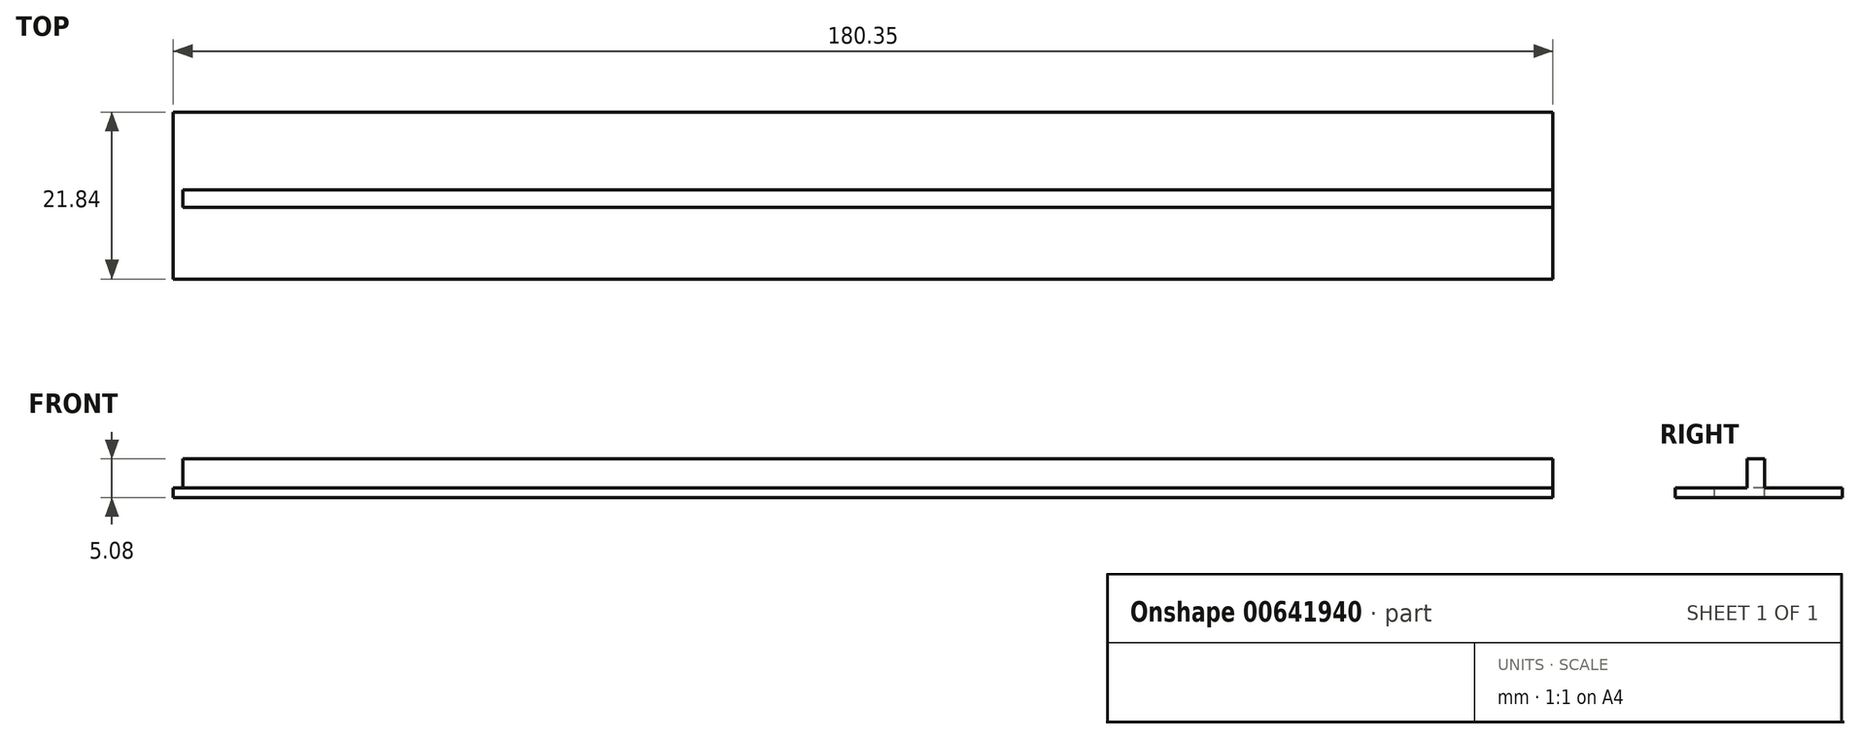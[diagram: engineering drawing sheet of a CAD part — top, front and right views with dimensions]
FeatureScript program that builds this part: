
annotation { "Feature Type Name" : "Feature", "Feature Type Description" : "" }
export const myFeature = defineFeature(function(context is Context, id is Id, definition is map)
    precondition{}
    {
        {
            var Q0;
            Q0=qCreatedBy(makeId("Front.planeOp"),FACE);
            var sketch = newSketch(context, id + "F0", { "sketchPlane" : qUnion([Q0])});
            skLineSegment(sketch, "E0.bottom", {"start": v(107.95, -50.8) * mm, "end": v(-107.95, -50.8) * mm});
            skLineSegment(sketch, "E0.top", {"start": v(107.95, 50.8) * mm, "end": v(-107.95, 50.8) * mm});
            skLineSegment(sketch, "E0.left", {"start": v(107.95, -50.8) * mm, "end": v(107.95, 50.8) * mm});
            skLineSegment(sketch, "E0.right", {"start": v(-107.95, -50.8) * mm, "end": v(-107.95, 50.8) * mm});
            skPoint(sketch, "E0.middle", {"position": v(0, 0) * mm});
            skLineSegment(sketch, "E1.bottom", {"start": v(88.9, -31.75) * mm, "end": v(-88.9, -31.75) * mm});
            skLineSegment(sketch, "E1.top", {"start": v(88.9, 31.75) * mm, "end": v(-88.9, 31.75) * mm});
            skLineSegment(sketch, "E1.left", {"start": v(88.9, -31.75) * mm, "end": v(88.9, 31.75) * mm});
            skLineSegment(sketch, "E1.right", {"start": v(-88.9, -31.75) * mm, "end": v(-88.9, 31.75) * mm});
            skSolve(sketch);
        }
        {
            var Q0;
            Q0=makeQuery(id+"F0.imprint","IMPRINT",FACE,{"disambiguationData":[TD([[makeQuery(id+"F0.imprint","IMPRINT",EDGE,{"derivedFrom":sQuery(id+"F0.wireOp",EDGE,"E0.bottom")}),-1.0]])]});
            extrude(context, id + "F1", {"entities" : qUnion([Q0]), "depth" : 12.7 * mm});
        }
        {
            var Q0;
            Q0=makeQuery(id+"F1.opExtrude","SWEPT_FACE",FACE,{"disambiguationData":[OSD([sQuery(id+"F0.wireOp",EDGE,"E0.top")])]});
            var sketch = newSketch(context, id + "F2", { "sketchPlane" : qUnion([Q0])});
            skLineSegment(sketch, "E2", {"start": v(-75.05, 0) * mm, "end": v(-80.97, -12.7) * mm});
            skLineSegment(sketch, "E3", {"start": v(-80.97, -12.7) * mm, "end": v(-78.17, -12.7) * mm});
            skLineSegment(sketch, "E4", {"start": v(-78.17, -12.7) * mm, "end": v(-72.25, 0) * mm});
            skLineSegment(sketch, "E5", {"start": v(-72.25, 0) * mm, "end": v(-75.05, 0) * mm});
            skLineSegment(sketch, "E6.1.0.0", {"start": v(-64.33, 0) * mm, "end": v(-70.25, -12.7) * mm});
            skLineSegment(sketch, "E6.1.0.1", {"start": v(-70.25, -12.7) * mm, "end": v(-67.45, -12.7) * mm});
            skLineSegment(sketch, "E6.1.0.2", {"start": v(-67.45, -12.7) * mm, "end": v(-61.53, 0) * mm});
            skLineSegment(sketch, "E6.1.0.3", {"start": v(-61.53, 0) * mm, "end": v(-64.33, 0) * mm});
            skLineSegment(sketch, "E6.2.0.0", {"start": v(-53.6, 0) * mm, "end": v(-59.53, -12.7) * mm});
            skLineSegment(sketch, "E6.2.0.1", {"start": v(-59.53, -12.7) * mm, "end": v(-56.73, -12.7) * mm});
            skLineSegment(sketch, "E6.2.0.2", {"start": v(-56.73, -12.7) * mm, "end": v(-50.8, 0) * mm});
            skLineSegment(sketch, "E6.2.0.3", {"start": v(-50.8, 0) * mm, "end": v(-53.6, 0) * mm});
            skLineSegment(sketch, "E6.3.0.0", {"start": v(-42.88, 0) * mm, "end": v(-48.8, -12.7) * mm});
            skLineSegment(sketch, "E6.3.0.1", {"start": v(-48.8, -12.7) * mm, "end": v(-46, -12.7) * mm});
            skLineSegment(sketch, "E6.3.0.2", {"start": v(-46, -12.7) * mm, "end": v(-40.08, 0) * mm});
            skLineSegment(sketch, "E6.3.0.3", {"start": v(-40.08, 0) * mm, "end": v(-42.88, 0) * mm});
            skLineSegment(sketch, "E6.4.0.0", {"start": v(-32.16, 0) * mm, "end": v(-38.08, -12.7) * mm});
            skLineSegment(sketch, "E6.4.0.1", {"start": v(-38.08, -12.7) * mm, "end": v(-35.28, -12.7) * mm});
            skLineSegment(sketch, "E6.4.0.2", {"start": v(-35.28, -12.7) * mm, "end": v(-29.36, 0) * mm});
            skLineSegment(sketch, "E6.4.0.3", {"start": v(-29.36, 0) * mm, "end": v(-32.16, 0) * mm});
            skLineSegment(sketch, "E6.5.0.0", {"start": v(-21.44, 0) * mm, "end": v(-27.36, -12.7) * mm});
            skLineSegment(sketch, "E6.5.0.1", {"start": v(-27.36, -12.7) * mm, "end": v(-24.56, -12.7) * mm});
            skLineSegment(sketch, "E6.5.0.2", {"start": v(-24.56, -12.7) * mm, "end": v(-18.64, 0) * mm});
            skLineSegment(sketch, "E6.5.0.3", {"start": v(-18.64, 0) * mm, "end": v(-21.44, 0) * mm});
            skLineSegment(sketch, "E6.6.0.0", {"start": v(-10.72, 0) * mm, "end": v(-16.64, -12.7) * mm});
            skLineSegment(sketch, "E6.6.0.1", {"start": v(-16.64, -12.7) * mm, "end": v(-13.84, -12.7) * mm});
            skLineSegment(sketch, "E6.6.0.2", {"start": v(-13.84, -12.7) * mm, "end": v(-7.92, 0) * mm});
            skLineSegment(sketch, "E6.6.0.3", {"start": v(-7.92, 0) * mm, "end": v(-10.72, 0) * mm});
            skLineSegment(sketch, "E6.direction1", {"start": v(-80.97, -12.7) * mm, "end": v(-70.25, -12.7) * mm, "construction": true});
            skLineSegment(sketch, "E7", {"start": v(75.05, 0) * mm, "end": v(80.97, -12.7) * mm});
            skLineSegment(sketch, "E8", {"start": v(80.97, -12.7) * mm, "end": v(78.17, -12.7) * mm});
            skLineSegment(sketch, "E9", {"start": v(78.17, -12.7) * mm, "end": v(72.25, 0) * mm});
            skLineSegment(sketch, "E10", {"start": v(72.25, 0) * mm, "end": v(75.05, 0) * mm});
            skLineSegment(sketch, "E11.1.0.0", {"start": v(70.25, -12.7) * mm, "end": v(67.45, -12.7) * mm});
            skLineSegment(sketch, "E11.1.0.1", {"start": v(64.33, 0) * mm, "end": v(70.25, -12.7) * mm});
            skLineSegment(sketch, "E11.1.0.2", {"start": v(61.53, 0) * mm, "end": v(64.33, 0) * mm});
            skLineSegment(sketch, "E11.1.0.3", {"start": v(67.45, -12.7) * mm, "end": v(61.53, 0) * mm});
            skLineSegment(sketch, "E11.2.0.0", {"start": v(59.53, -12.7) * mm, "end": v(56.73, -12.7) * mm});
            skLineSegment(sketch, "E11.2.0.1", {"start": v(53.6, 0) * mm, "end": v(59.53, -12.7) * mm});
            skLineSegment(sketch, "E11.2.0.2", {"start": v(50.8, 0) * mm, "end": v(53.6, 0) * mm});
            skLineSegment(sketch, "E11.2.0.3", {"start": v(56.73, -12.7) * mm, "end": v(50.8, 0) * mm});
            skLineSegment(sketch, "E11.3.0.0", {"start": v(48.8, -12.7) * mm, "end": v(46, -12.7) * mm});
            skLineSegment(sketch, "E11.3.0.1", {"start": v(42.88, 0) * mm, "end": v(48.8, -12.7) * mm});
            skLineSegment(sketch, "E11.3.0.2", {"start": v(40.08, 0) * mm, "end": v(42.88, 0) * mm});
            skLineSegment(sketch, "E11.3.0.3", {"start": v(46, -12.7) * mm, "end": v(40.08, 0) * mm});
            skLineSegment(sketch, "E11.4.0.0", {"start": v(38.08, -12.7) * mm, "end": v(35.28, -12.7) * mm});
            skLineSegment(sketch, "E11.4.0.1", {"start": v(32.16, 0) * mm, "end": v(38.08, -12.7) * mm});
            skLineSegment(sketch, "E11.4.0.2", {"start": v(29.36, 0) * mm, "end": v(32.16, 0) * mm});
            skLineSegment(sketch, "E11.4.0.3", {"start": v(35.28, -12.7) * mm, "end": v(29.36, 0) * mm});
            skLineSegment(sketch, "E11.5.0.0", {"start": v(27.36, -12.7) * mm, "end": v(24.56, -12.7) * mm});
            skLineSegment(sketch, "E11.5.0.1", {"start": v(21.44, 0) * mm, "end": v(27.36, -12.7) * mm});
            skLineSegment(sketch, "E11.5.0.2", {"start": v(18.64, 0) * mm, "end": v(21.44, 0) * mm});
            skLineSegment(sketch, "E11.5.0.3", {"start": v(24.56, -12.7) * mm, "end": v(18.64, 0) * mm});
            skLineSegment(sketch, "E11.6.0.0", {"start": v(16.64, -12.7) * mm, "end": v(13.84, -12.7) * mm});
            skLineSegment(sketch, "E11.6.0.1", {"start": v(10.72, 0) * mm, "end": v(16.64, -12.7) * mm});
            skLineSegment(sketch, "E11.6.0.2", {"start": v(7.92, 0) * mm, "end": v(10.72, 0) * mm});
            skLineSegment(sketch, "E11.6.0.3", {"start": v(13.84, -12.7) * mm, "end": v(7.92, 0) * mm});
            skLineSegment(sketch, "E11.direction1", {"start": v(78.17, -12.7) * mm, "end": v(67.45, -12.7) * mm, "construction": true});
            skLineSegment(sketch, "E12", {"start": v(0, 0) * mm, "end": v(0, -12.7) * mm, "construction": true});
            skLineSegment(sketch, "E13", {"start": v(0, 0) * mm, "end": v(-5.92, -12.7) * mm});
            skLineSegment(sketch, "E14", {"start": v(0, 0) * mm, "end": v(5.92, -12.7) * mm});
            skLineSegment(sketch, "E15", {"start": v(-5.92, -12.7) * mm, "end": v(5.92, -12.7) * mm});
            skSolve(sketch);
        }
        {
            var Q0;
            Q0=qSketchRegion(id+"F2",true);
            extrude(context, id + "F3", {"entities" : qUnion([Q0]), "operationType" : NewBodyOperationType.ADD, "oppositeDirection" : true, "depth" : 101.6 * mm});
        }
        {
            var Q0;
            Q0=makeQuery(id+"F1.opExtrude","CAP_EDGE",EDGE,{"disambiguationData":[OSD([sQuery(id+"F0.wireOp",EDGE,"E0.top")])],"isStart":false});
            var Q1;
            Q1=makeQuery(id+"F1.opExtrude","CAP_EDGE",EDGE,{"disambiguationData":[OSD([sQuery(id+"F0.wireOp",EDGE,"E0.right")])],"isStart":false});
            var Q2;
            Q2=makeQuery(id+"F1.opExtrude","CAP_EDGE",EDGE,{"disambiguationData":[OSD([sQuery(id+"F0.wireOp",EDGE,"E0.bottom")])],"isStart":false});
            var Q3;
            Q3=makeQuery(id+"F1.opExtrude","CAP_EDGE",EDGE,{"disambiguationData":[OSD([sQuery(id+"F0.wireOp",EDGE,"E0.left")])],"isStart":false});
            fillet(context, id + "F4", {"entities" : qUnion([Q0, Q1, Q2, Q3]), "radius" : 12.7 * mm, "tangentPropagation" : true, "allowEdgeOverflow" : false});
        }
        {
            var Q0;
            Q0=makeQuery(id+"F3.boolean.opBoolean","MERGE",FACE,{"derivedFrom":[makeQuery(id+"F1.opExtrude","CAP_FACE",FACE,{"disambiguationData":[OSD([sQuery(id+"F0.wireOp",EDGE,"E0.bottom"),sQuery(id+"F0.wireOp",EDGE,"E0.top"),sQuery(id+"F0.wireOp",EDGE,"E0.left"),sQuery(id+"F0.wireOp",EDGE,"E0.right"),sQuery(id+"F0.wireOp",EDGE,"E1.bottom"),sQuery(id+"F0.wireOp",EDGE,"E1.top"),sQuery(id+"F0.wireOp",EDGE,"E1.left"),sQuery(id+"F0.wireOp",EDGE,"E1.right")])],"isStart":true}),makeQuery(id+"F3.opExtrude","SWEPT_FACE",FACE,{"disambiguationData":[OSD([sQuery(id+"F2.wireOp",EDGE,"E5")])]}),makeQuery(id+"F3.opExtrude","SWEPT_FACE",FACE,{"disambiguationData":[OSD([sQuery(id+"F2.wireOp",EDGE,"E6.1.0.3")])]}),makeQuery(id+"F3.opExtrude","SWEPT_FACE",FACE,{"disambiguationData":[OSD([sQuery(id+"F2.wireOp",EDGE,"E6.2.0.3")])]}),makeQuery(id+"F3.opExtrude","SWEPT_FACE",FACE,{"disambiguationData":[OSD([sQuery(id+"F2.wireOp",EDGE,"E6.3.0.3")])]}),makeQuery(id+"F3.opExtrude","SWEPT_FACE",FACE,{"disambiguationData":[OSD([sQuery(id+"F2.wireOp",EDGE,"E6.4.0.3")])]}),makeQuery(id+"F3.opExtrude","SWEPT_FACE",FACE,{"disambiguationData":[OSD([sQuery(id+"F2.wireOp",EDGE,"E6.5.0.3")])]}),makeQuery(id+"F3.opExtrude","SWEPT_FACE",FACE,{"disambiguationData":[OSD([sQuery(id+"F2.wireOp",EDGE,"E6.6.0.3")])]}),makeQuery(id+"F3.opExtrude","SWEPT_FACE",FACE,{"disambiguationData":[OSD([sQuery(id+"F2.wireOp",EDGE,"E10")])]}),makeQuery(id+"F3.opExtrude","SWEPT_FACE",FACE,{"disambiguationData":[OSD([sQuery(id+"F2.wireOp",EDGE,"E11.1.0.2")])]}),makeQuery(id+"F3.opExtrude","SWEPT_FACE",FACE,{"disambiguationData":[OSD([sQuery(id+"F2.wireOp",EDGE,"E11.2.0.2")])]}),makeQuery(id+"F3.opExtrude","SWEPT_FACE",FACE,{"disambiguationData":[OSD([sQuery(id+"F2.wireOp",EDGE,"E11.3.0.2")])]}),makeQuery(id+"F3.opExtrude","SWEPT_FACE",FACE,{"disambiguationData":[OSD([sQuery(id+"F2.wireOp",EDGE,"E11.4.0.2")])]}),makeQuery(id+"F3.opExtrude","SWEPT_FACE",FACE,{"disambiguationData":[OSD([sQuery(id+"F2.wireOp",EDGE,"E11.5.0.2")])]}),makeQuery(id+"F3.opExtrude","SWEPT_FACE",FACE,{"disambiguationData":[OSD([sQuery(id+"F2.wireOp",EDGE,"E11.6.0.2")])]})]});
            var sketch = newSketch(context, id + "F5", { "sketchPlane" : qUnion([Q0])});
            skLineSegment(sketch, "E16.bottom", {"start": v(90.17, -33.02) * mm, "end": v(-90.17, -33.02) * mm});
            skLineSegment(sketch, "E16.top", {"start": v(90.17, 33.02) * mm, "end": v(-90.17, 33.02) * mm});
            skLineSegment(sketch, "E16.right", {"start": v(-90.17, -33.02) * mm, "end": v(-90.17, 33.02) * mm});
            skPoint(sketch, "E16.middle", {"position": v(0, 0) * mm});
            skLineSegment(sketch, "E17.bottom", {"start": v(88.9, -31.75) * mm, "end": v(-88.9, -31.75) * mm});
            skLineSegment(sketch, "E17.top", {"start": v(88.9, 31.75) * mm, "end": v(-88.9, 31.75) * mm});
            skLineSegment(sketch, "E17.right", {"start": v(-88.9, -31.75) * mm, "end": v(-88.9, 31.75) * mm});
            skLineSegment(sketch, "E18", {"start": v(88.9, 31.75) * mm, "end": v(90.17, 31.75) * mm});
            skLineSegment(sketch, "E19", {"start": v(90.17, 31.75) * mm, "end": v(90.17, 33.02) * mm});
            skLineSegment(sketch, "E20", {"start": v(88.9, -31.75) * mm, "end": v(90.17, -31.75) * mm});
            skLineSegment(sketch, "E21", {"start": v(90.17, -31.75) * mm, "end": v(90.17, -33.02) * mm});
            skSolve(sketch);
        }
        {
            var Q0;
            Q0=qSketchRegion(id+"F5",true);
            extrude(context, id + "F6", {"entities" : qUnion([Q0]), "operationType" : NewBodyOperationType.ADD, "depth" : 3.3 * mm});
        }
        {
            var Q0;
            Q0=makeQuery(id+"F6.opExtrude","CAP_FACE",FACE,{"disambiguationData":[OSD([sQuery(id+"F5.wireOp",EDGE,"E16.bottom"),sQuery(id+"F5.wireOp",EDGE,"E16.top"),sQuery(id+"F5.wireOp",EDGE,"E16.right"),sQuery(id+"F5.wireOp",EDGE,"E17.bottom"),sQuery(id+"F5.wireOp",EDGE,"E17.top"),sQuery(id+"F5.wireOp",EDGE,"E17.right"),sQuery(id+"F5.wireOp",EDGE,"E18"),sQuery(id+"F5.wireOp",EDGE,"E19"),sQuery(id+"F5.wireOp",EDGE,"E20"),sQuery(id+"F5.wireOp",EDGE,"E21")])],"isStart":false});
            var sketch = newSketch(context, id + "F7", { "sketchPlane" : qUnion([Q0])});
            skLineSegment(sketch, "E22.bottom", {"start": v(-90.17, 33.02) * mm, "end": v(88.9, 33.02) * mm});
            skLineSegment(sketch, "E22.top", {"start": v(-90.17, -33.02) * mm, "end": v(88.9, -33.02) * mm});
            skLineSegment(sketch, "E22.left", {"start": v(-90.17, 33.02) * mm, "end": v(-90.17, -33.02) * mm});
            skLineSegment(sketch, "E22.right", {"start": v(88.9, 33.02) * mm, "end": v(88.9, -33.02) * mm});
            skLineSegment(sketch, "E23.bottom", {"start": v(-86.36, 27.94) * mm, "end": v(86.36, 27.94) * mm});
            skLineSegment(sketch, "E23.top", {"start": v(-86.36, -27.94) * mm, "end": v(86.36, -27.94) * mm});
            skLineSegment(sketch, "E23.left", {"start": v(-86.36, 27.94) * mm, "end": v(-86.36, -27.94) * mm});
            skLineSegment(sketch, "E23.right", {"start": v(86.36, 27.94) * mm, "end": v(86.36, -27.94) * mm});
            skSolve(sketch);
        }
        {
            var Q0;
            Q0=qSketchRegion(id+"F7",true);
            extrude(context, id + "F8", {"entities" : qUnion([Q0]), "operationType" : NewBodyOperationType.ADD, "depth" : 1.78 * mm});
        }
        {
            var Q0;
            Q0=makeQuery(id+"F8.opExtrude","CAP_FACE",FACE,{"disambiguationData":[OSD([sQuery(id+"F7.wireOp",EDGE,"E22.bottom"),sQuery(id+"F7.wireOp",EDGE,"E22.top"),sQuery(id+"F7.wireOp",EDGE,"E22.left"),sQuery(id+"F7.wireOp",EDGE,"E22.right"),sQuery(id+"F7.wireOp",EDGE,"E23.bottom"),sQuery(id+"F7.wireOp",EDGE,"E23.top"),sQuery(id+"F7.wireOp",EDGE,"E23.left"),sQuery(id+"F7.wireOp",EDGE,"E23.right")])],"isStart":false});
            var sketch = newSketch(context, id + "F9", { "sketchPlane" : qUnion([Q0])});
            skLineSegment(sketch, "E24.bottom", {"start": v(-90.17, 33.02) * mm, "end": v(88.9, 33.02) * mm});
            skLineSegment(sketch, "E24.top", {"start": v(-90.17, -33.02) * mm, "end": v(88.9, -33.02) * mm});
            skLineSegment(sketch, "E24.left", {"start": v(-90.17, 33.02) * mm, "end": v(-90.17, -33.02) * mm});
            skLineSegment(sketch, "E25.bottom", {"start": v(-88.9, 31.75) * mm, "end": v(87.63, 31.75) * mm});
            skLineSegment(sketch, "E25.top", {"start": v(-88.9, -31.75) * mm, "end": v(87.63, -31.75) * mm});
            skLineSegment(sketch, "E25.left", {"start": v(-88.9, 31.75) * mm, "end": v(-88.9, -31.75) * mm});
            skLineSegment(sketch, "E26", {"start": v(88.9, -33.02) * mm, "end": v(90.18, -33.02) * mm});
            skLineSegment(sketch, "E27", {"start": v(90.18, -33.02) * mm, "end": v(90.18, -31.75) * mm});
            skLineSegment(sketch, "E28", {"start": v(90.18, -31.75) * mm, "end": v(87.63, -31.75) * mm});
            skLineSegment(sketch, "E29", {"start": v(88.9, 33.02) * mm, "end": v(90.17, 33.02) * mm});
            skLineSegment(sketch, "E30", {"start": v(90.17, 33.02) * mm, "end": v(90.17, 31.75) * mm});
            skLineSegment(sketch, "E31", {"start": v(90.17, 31.75) * mm, "end": v(87.63, 31.75) * mm});
            skSolve(sketch);
        }
        {
            var Q0;
            {var subQ5=sQuery(id+"F9.wireOp",EDGE,"E24.bottom");Q0=makeQuery(id+"F9.imprint","IMPRINT",FACE,{"disambiguationData":[TD([[makeQuery(id+"F9.imprint","IMPRINT",EDGE,{"derivedFrom":subQ5}),1.0]])]});}
            var Q1;
            {var subQ0=sQuery(id+"F9.wireOp",EDGE,"E29");Q1=makeQuery(id+"F9.imprint","IMPRINT",FACE,{"disambiguationData":[TD([[makeQuery(id+"F9.imprint","IMPRINT",EDGE,{"derivedFrom":subQ0}),-1.0]])]});}
            var Q2;
            {var subQ0=sQuery(id+"F9.wireOp",EDGE,"E26");Q2=makeQuery(id+"F9.imprint","IMPRINT",FACE,{"disambiguationData":[TD([[makeQuery(id+"F9.imprint","IMPRINT",EDGE,{"derivedFrom":subQ0}),1.0]])]});}
            extrude(context, id + "F10", {"entities" : qUnion([Q0, Q1, Q2]), "operationType" : NewBodyOperationType.ADD, "depth" : 4.32 * mm});
        }
        {
            var Q0;
            {var subQ0=sQuery(id+"F5.wireOp",EDGE,"E21");var subQ1=sQuery(id+"F5.wireOp",EDGE,"E20");var subQ2=sQuery(id+"F5.wireOp",EDGE,"E17.bottom");var subQ3=sQuery(id+"F5.wireOp",EDGE,"E16.bottom");Q0=makeQuery(id+"F8.boolean.opBoolean","SPLIT",FACE,{"disambiguationData":[TD([makeQuery(id+"F1.opExtrude","SWEPT_FACE",FACE,{"disambiguationData":[OSD([sQuery(id+"F0.wireOp",EDGE,"E1.bottom")])]})])],"derivedFrom":makeQuery(id+"F6.opExtrude","CAP_FACE",FACE,{"disambiguationData":[OSD([subQ3,sQuery(id+"F5.wireOp",EDGE,"E16.top"),sQuery(id+"F5.wireOp",EDGE,"E16.right"),subQ2,sQuery(id+"F5.wireOp",EDGE,"E17.top"),sQuery(id+"F5.wireOp",EDGE,"E17.right"),sQuery(id+"F5.wireOp",EDGE,"E18"),sQuery(id+"F5.wireOp",EDGE,"E19"),subQ1,subQ0])],"isStart":false})});}
            var sketch = newSketch(context, id + "F11", { "sketchPlane" : qUnion([Q0])});
            skLineSegment(sketch, "E32.bottom", {"start": v(88.9, -33.02) * mm, "end": v(90.17, -33.02) * mm});
            skLineSegment(sketch, "E32.top", {"start": v(88.9, -31.75) * mm, "end": v(90.17, -31.75) * mm});
            skLineSegment(sketch, "E32.left", {"start": v(88.9, -33.02) * mm, "end": v(88.9, -31.75) * mm});
            skLineSegment(sketch, "E32.right", {"start": v(90.17, -33.02) * mm, "end": v(90.17, -31.75) * mm});
            skSolve(sketch);
        }
        {
            var Q0;
            Q0=qSketchRegion(id+"F11",true);
            extrude(context, id + "F12", {"entities" : qUnion([Q0]), "operationType" : NewBodyOperationType.ADD, "depth" : 1.78 * mm});
        }
        {
            var Q0;
            Q0=makeQuery(id+"F10.opExtrude","CAP_FACE",FACE,{"disambiguationData":[OSD([sQuery(id+"F9.wireOp",EDGE,"E24.bottom"),sQuery(id+"F9.wireOp",EDGE,"E24.top"),sQuery(id+"F9.wireOp",EDGE,"E24.left"),sQuery(id+"F9.wireOp",EDGE,"E25.bottom"),sQuery(id+"F9.wireOp",EDGE,"E25.top"),sQuery(id+"F9.wireOp",EDGE,"E25.left"),sQuery(id+"F9.wireOp",EDGE,"E26"),sQuery(id+"F9.wireOp",EDGE,"E27"),sQuery(id+"F9.wireOp",EDGE,"E28"),sQuery(id+"F9.wireOp",EDGE,"E29"),sQuery(id+"F9.wireOp",EDGE,"E30"),sQuery(id+"F9.wireOp",EDGE,"E31")])],"isStart":false});
            var sketch = newSketch(context, id + "F13", { "sketchPlane" : qUnion([Q0])});
            skLineSegment(sketch, "E33.bottom", {"start": v(-90.17, 33.02) * mm, "end": v(88.9, 33.02) * mm});
            skLineSegment(sketch, "E33.top", {"start": v(-90.17, -33.02) * mm, "end": v(88.9, -33.02) * mm});
            skLineSegment(sketch, "E34.bottom", {"start": v(-84.84, 27.94) * mm, "end": v(88.9, 27.94) * mm});
            skLineSegment(sketch, "E34.top", {"start": v(-84.84, -27.94) * mm, "end": v(88.9, -27.94) * mm});
            skLineSegment(sketch, "E35", {"start": v(-84.84, 27.94) * mm, "end": v(-90.17, 27.94) * mm});
            skLineSegment(sketch, "E36", {"start": v(-90.17, 27.94) * mm, "end": v(-90.17, 33.02) * mm});
            skLineSegment(sketch, "E37", {"start": v(-84.84, -27.94) * mm, "end": v(-90.17, -27.94) * mm});
            skLineSegment(sketch, "E38", {"start": v(-90.17, -27.94) * mm, "end": v(-90.17, -33.02) * mm});
            skLineSegment(sketch, "E39.bottom", {"start": v(-90.17, 27.94) * mm, "end": v(-88.9, 27.94) * mm});
            skLineSegment(sketch, "E39.top", {"start": v(-90.17, -27.94) * mm, "end": v(-88.9, -27.94) * mm});
            skLineSegment(sketch, "E39.left", {"start": v(-90.17, 27.94) * mm, "end": v(-90.17, -27.94) * mm});
            skLineSegment(sketch, "E39.right", {"start": v(-88.9, 27.94) * mm, "end": v(-88.9, -27.94) * mm});
            skLineSegment(sketch, "E40", {"start": v(88.9, -27.94) * mm, "end": v(88.9, -33.02) * mm});
            skLineSegment(sketch, "E41", {"start": v(88.9, 27.94) * mm, "end": v(88.9, 33.02) * mm});
            skSolve(sketch);
        }
        {
            var Q0;
            Q0=qSketchRegion(id+"F13",true);
            extrude(context, id + "F14", {"entities" : qUnion([Q0]), "operationType" : NewBodyOperationType.ADD, "depth" : 2.3 * mm});
        }
        {
            var Q0;
            Q0=makeQuery(id+"F14.opExtrude","SWEPT_FACE",FACE,{"disambiguationData":[OSD([sQuery(id+"F13.wireOp",EDGE,"E34.top"),sQuery(id+"F13.wireOp",EDGE,"E37"),sQuery(id+"F13.wireOp",EDGE,"TGxW7JvE-hO0u-tt39-ioUT-bYuH0o1wrKsi")])]});
            var sketch = newSketch(context, id + "F15", { "sketchPlane" : qUnion([Q0])});
            skSolve(sketch);
        }
        {
            var Q0;
            Q0=makeQuery(id+"Fv8F5Soem3vfvmW_1.boolean.opBoolean","MERGE",FACE,{"derivedFrom":[makeQuery(id+"F14.opExtrude","CAP_FACE",FACE,{"disambiguationData":[OSD([sQuery(id+"F13.wireOp",EDGE,"E33.bottom"),sQuery(id+"F13.wireOp",EDGE,"E33.top"),sQuery(id+"F13.wireOp",EDGE,"E34.bottom"),sQuery(id+"F13.wireOp",EDGE,"E34.top"),sQuery(id+"F13.wireOp",EDGE,"E35"),sQuery(id+"F13.wireOp",EDGE,"E36"),sQuery(id+"F13.wireOp",EDGE,"E37"),sQuery(id+"F13.wireOp",EDGE,"E38"),sQuery(id+"F13.wireOp",EDGE,"E39.left"),sQuery(id+"F13.wireOp",EDGE,"E39.right"),sQuery(id+"F13.wireOp",EDGE,"TGxW7JvE-hO0u-tt39-ioUT-bYuH0o1wrKsi"),sQuery(id+"F13.wireOp",EDGE,"xJwFBrmR-DKHQ-Ms6E-cGLF-1sDl0en4KIHk"),sQuery(id+"F13.wireOp",EDGE,"KjPjYPhn-M9NA-BWyU-6eae-7lh8KEkwCyoe"),sQuery(id+"F13.wireOp",EDGE,"DDPbrne3-7nOW-QVff-d2O1-u6GeuogKL0BI")])],"isStart":false}),makeQuery(id+"Fv8F5Soem3vfvmW_1.opExtrude","SWEPT_FACE",FACE,{"disambiguationData":[OSD([sQuery(id+"F15.wireOp",EDGE,"I5fvG48v-rP8C-mtnB-2jEv-sWBCkAZKz6mY.bottom")])]})]});
            var sketch = newSketch(context, id + "F16", { "sketchPlane" : qUnion([Q0])});
            skLineSegment(sketch, "E42.bottom", {"start": v(-90.17, 33.02) * mm, "end": v(90.17, 33.02) * mm});
            skLineSegment(sketch, "E42.top", {"start": v(-90.17, -33.02) * mm, "end": v(90.17, -33.02) * mm});
            skLineSegment(sketch, "E42.left", {"start": v(-90.17, 33.02) * mm, "end": v(-90.17, -33.02) * mm});
            skLineSegment(sketch, "E43.bottom", {"start": v(-88.9, 31.75) * mm, "end": v(84.62, 31.75) * mm});
            skLineSegment(sketch, "E43.top", {"start": v(-88.9, -31.75) * mm, "end": v(84.62, -31.75) * mm});
            skLineSegment(sketch, "E43.left", {"start": v(-88.9, 31.75) * mm, "end": v(-88.9, -31.75) * mm});
            skLineSegment(sketch, "E44", {"start": v(84.62, 31.75) * mm, "end": v(90.17, 31.75) * mm});
            skLineSegment(sketch, "E45", {"start": v(90.17, 33.02) * mm, "end": v(90.17, 31.75) * mm});
            skLineSegment(sketch, "E46", {"start": v(84.62, -31.75) * mm, "end": v(90.17, -31.75) * mm});
            skLineSegment(sketch, "E47", {"start": v(90.17, -33.02) * mm, "end": v(90.17, -31.75) * mm});
            skSolve(sketch);
        }
        {
            var Q0;
            Q0=qSketchRegion(id+"F16",true);
            extrude(context, id + "F17", {"entities" : qUnion([Q0]), "operationType" : NewBodyOperationType.ADD, "depth" : 10.16 * mm});
        }
        {
            var Q0;
            {var subQ0=sQuery(id+"F5.wireOp",EDGE,"E18");var subQ1=sQuery(id+"F5.wireOp",EDGE,"E17.top");var subQ2=sQuery(id+"F5.wireOp",EDGE,"E19");var subQ3=sQuery(id+"F5.wireOp",EDGE,"E16.top");Q0=makeQuery(id+"F8.boolean.opBoolean","SPLIT",FACE,{"disambiguationData":[TD([makeQuery(id+"F1.opExtrude","SWEPT_FACE",FACE,{"disambiguationData":[OSD([sQuery(id+"F0.wireOp",EDGE,"E1.top")])]})])],"derivedFrom":makeQuery(id+"F6.opExtrude","CAP_FACE",FACE,{"disambiguationData":[OSD([sQuery(id+"F5.wireOp",EDGE,"E16.bottom"),subQ3,sQuery(id+"F5.wireOp",EDGE,"E16.right"),sQuery(id+"F5.wireOp",EDGE,"E17.bottom"),subQ1,sQuery(id+"F5.wireOp",EDGE,"E17.right"),subQ0,subQ2,sQuery(id+"F5.wireOp",EDGE,"E20"),sQuery(id+"F5.wireOp",EDGE,"E21")])],"isStart":false})});}
            var sketch = newSketch(context, id + "F18", { "sketchPlane" : qUnion([Q0])});
            skLineSegment(sketch, "E48.bottom", {"start": v(88.9, 33.02) * mm, "end": v(90.17, 33.02) * mm});
            skLineSegment(sketch, "E48.top", {"start": v(88.9, 31.75) * mm, "end": v(90.17, 31.75) * mm});
            skLineSegment(sketch, "E48.left", {"start": v(88.9, 33.02) * mm, "end": v(88.9, 31.75) * mm});
            skLineSegment(sketch, "E48.right", {"start": v(90.17, 33.02) * mm, "end": v(90.17, 31.75) * mm});
            skSolve(sketch);
        }
        {
            var Q0;
            Q0=qSketchRegion(id+"F18",true);
            extrude(context, id + "F19", {"entities" : qUnion([Q0]), "operationType" : NewBodyOperationType.ADD, "depth" : 1.78 * mm});
        }
        {
            var Q0;
            {var subQ0=sQuery(id+"F9.wireOp",EDGE,"E27");var subQ1=sQuery(id+"F9.wireOp",EDGE,"E26");var subQ2=sQuery(id+"F9.wireOp",EDGE,"E24.top");var subQ4=sQuery(id+"F9.wireOp",EDGE,"E28");Q0=makeQuery(id+"F14.boolean.opBoolean","SPLIT",FACE,{"disambiguationData":[TD([makeQuery(id+"F6.opExtrude","SWEPT_FACE",FACE,{"disambiguationData":[OSD([sQuery(id+"F5.wireOp",EDGE,"E16.bottom")])]})])],"derivedFrom":makeQuery(id+"F10.opExtrude","CAP_FACE",FACE,{"disambiguationData":[OSD([sQuery(id+"F9.wireOp",EDGE,"E24.bottom"),subQ2,sQuery(id+"F9.wireOp",EDGE,"E24.left"),sQuery(id+"F9.wireOp",EDGE,"E25.bottom"),sQuery(id+"F9.wireOp",EDGE,"E25.top"),sQuery(id+"F9.wireOp",EDGE,"E25.left"),subQ1,subQ0,subQ4,sQuery(id+"F9.wireOp",EDGE,"E29"),sQuery(id+"F9.wireOp",EDGE,"E30"),sQuery(id+"F9.wireOp",EDGE,"E31")])],"isStart":false})});}
            var sketch = newSketch(context, id + "F20", { "sketchPlane" : qUnion([Q0])});
            skLineSegment(sketch, "E49.bottom", {"start": v(88.9, -33.02) * mm, "end": v(90.18, -33.02) * mm});
            skLineSegment(sketch, "E49.top", {"start": v(88.9, -31.75) * mm, "end": v(90.18, -31.75) * mm});
            skLineSegment(sketch, "E49.left", {"start": v(88.9, -33.02) * mm, "end": v(88.9, -31.75) * mm});
            skLineSegment(sketch, "E49.right", {"start": v(90.18, -33.02) * mm, "end": v(90.18, -31.75) * mm});
            skSolve(sketch);
        }
        {
            var Q0;
            {var subQ2=sQuery(id+"F9.wireOp",EDGE,"E30");var subQ3=sQuery(id+"F9.wireOp",EDGE,"E29");var subQ4=sQuery(id+"F9.wireOp",EDGE,"E24.bottom");var subQ5=sQuery(id+"F9.wireOp",EDGE,"E31");Q0=makeQuery(id+"F14.boolean.opBoolean","SPLIT",FACE,{"disambiguationData":[TD([makeQuery(id+"F6.opExtrude","SWEPT_FACE",FACE,{"disambiguationData":[OSD([sQuery(id+"F5.wireOp",EDGE,"E16.top")])]})])],"derivedFrom":makeQuery(id+"F10.opExtrude","CAP_FACE",FACE,{"disambiguationData":[OSD([subQ4,sQuery(id+"F9.wireOp",EDGE,"E24.top"),sQuery(id+"F9.wireOp",EDGE,"E24.left"),sQuery(id+"F9.wireOp",EDGE,"E25.bottom"),sQuery(id+"F9.wireOp",EDGE,"E25.top"),sQuery(id+"F9.wireOp",EDGE,"E25.left"),sQuery(id+"F9.wireOp",EDGE,"E26"),sQuery(id+"F9.wireOp",EDGE,"E27"),sQuery(id+"F9.wireOp",EDGE,"E28"),subQ3,subQ2,subQ5])],"isStart":false})});}
            var sketch = newSketch(context, id + "F21", { "sketchPlane" : qUnion([Q0])});
            skLineSegment(sketch, "E50.bottom", {"start": v(88.9, 31.75) * mm, "end": v(90.17, 31.75) * mm});
            skLineSegment(sketch, "E50.top", {"start": v(88.9, 33.02) * mm, "end": v(90.17, 33.02) * mm});
            skLineSegment(sketch, "E50.left", {"start": v(88.9, 31.75) * mm, "end": v(88.9, 33.02) * mm});
            skLineSegment(sketch, "E50.right", {"start": v(90.17, 31.75) * mm, "end": v(90.17, 33.02) * mm});
            skSolve(sketch);
        }
        {
            var Q0;
            Q0=qSketchRegion(id+"F21",true);
            var Q1;
            Q1=qSketchRegion(id+"F20",true);
            extrude(context, id + "F22", {"entities" : qUnion([Q0, Q1]), "operationType" : NewBodyOperationType.ADD, "depth" : 2.3 * mm});
        }
        {
            var Q0;
            Q0=makeQuery(id+"F12.boolean.opBoolean","MERGE",FACE,{"derivedFrom":[makeQuery(id+"F6.opExtrude","SWEPT_FACE",FACE,{"disambiguationData":[OSD([sQuery(id+"F5.wireOp",EDGE,"E21")])]}),makeQuery(id+"F12.opExtrude","SWEPT_FACE",FACE,{"disambiguationData":[OSD([sQuery(id+"F11.wireOp",EDGE,"E32.right")])]})]});
            var sketch = newSketch(context, id + "F23", { "sketchPlane" : qUnion([Q0])});
            skLineSegment(sketch, "E51.0.6", {"start": v(-21.84, 31.75) * mm, "end": v(-21.84, -31.75) * mm});
            skLineSegment(sketch, "E51.0.7", {"start": v(-21.84, -31.75) * mm, "end": v(-11.68, -31.75) * mm});
            skLineSegment(sketch, "E51.0.8", {"start": v(-11.68, -31.75) * mm, "end": v(-11.68, -27.94) * mm});
            skLineSegment(sketch, "E51.0.9", {"start": v(-11.68, -27.94) * mm, "end": v(-9.4, -27.94) * mm});
            skLineSegment(sketch, "E51.0.10", {"start": v(-9.4, -27.94) * mm, "end": v(-9.4, -31.75) * mm});
            skLineSegment(sketch, "E51.0.11", {"start": v(-9.4, -31.75) * mm, "end": v(-5.08, -31.75) * mm});
            skLineSegment(sketch, "E52.0.2", {"start": v(-21.84, 33.02) * mm, "end": v(-21.84, 31.75) * mm});
            skLineSegment(sketch, "E53.0.0", {"start": v(0, 31.75) * mm, "end": v(0, 33.02) * mm});
            skLineSegment(sketch, "E54.0.2", {"start": v(-5.08, -31.75) * mm, "end": v(-3.3, -31.75) * mm});
            skLineSegment(sketch, "E55.0", {"start": v(0, -50.8) * mm, "end": v(0, 50.8) * mm});
            skLineSegment(sketch, "E56", {"start": v(0, -50.8) * mm, "end": v(15.56, -50.8) * mm});
            skLineSegment(sketch, "E57", {"start": v(15.56, -50.8) * mm, "end": v(15.56, 54.86) * mm});
            skLineSegment(sketch, "E58", {"start": v(15.56, 54.86) * mm, "end": v(0, 50.8) * mm});
            skLineSegment(sketch, "E59.bottom", {"start": v(-21.84, 36.42) * mm, "end": v(0, 36.42) * mm});
            skLineSegment(sketch, "E59.top", {"start": v(-21.84, -31.75) * mm, "end": v(0, -31.75) * mm});
            skLineSegment(sketch, "E59.left", {"start": v(-21.84, 36.42) * mm, "end": v(-21.84, -31.75) * mm});
            skLineSegment(sketch, "E59.right", {"start": v(0, 36.42) * mm, "end": v(0, -31.75) * mm});
            skSolve(sketch);
        }
        {
            var Q0;
            {var subQ6=sQuery(id+"F23.wireOp",EDGE,"E56");Q0=makeQuery(id+"F23.imprint","IMPRINT",FACE,{"disambiguationData":[TD([[makeQuery(id+"F23.imprint","IMPRINT",EDGE,{"derivedFrom":subQ6}),1.0]])]});}
            var Q1;
            {var subQ9=sQuery(id+"F23.wireOp",EDGE,"E51.0.8");Q1=makeQuery(id+"F23.imprint","IMPRINT",FACE,{"disambiguationData":[TD([[makeQuery(id+"F23.imprint","IMPRINT",EDGE,{"derivedFrom":subQ9}),1.0]])]});}
            extrude(context, id + "F24", {"entities" : qUnion([Q0, Q1]), "operationType" : NewBodyOperationType.REMOVE, "endBound" : BoundingType.THROUGH_ALL, "oppositeDirection" : true, "depth" : 25.4 * mm, "hasSecondDirection" : true, "secondDirectionBound" : SecondDirectionBoundingType.THROUGH_ALL, "secondDirectionOppositeDirection" : false, "secondDirectionDepth" : 25.4 * mm});
        }
    });
